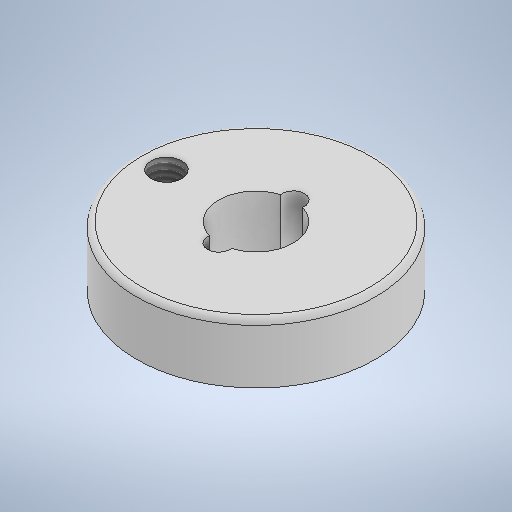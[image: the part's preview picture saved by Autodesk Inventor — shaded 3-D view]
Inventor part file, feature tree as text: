
AUTODESK INVENTOR PART (.ipt)
format: ipt  version: 2025.1 (Build 291241000, 241)  size: 259,072 bytes
history: native  units: mm
features: sketch x3, extrude x2, hole x1, fillet x1
ambient origin geometry x8: Origin, YZ Plane, XZ Plane, XY Plane, X Axis, Y Axis, Z Axis, Center Point
bodies: Solid1 (feature_tree)
feature tree (7):
  extrude  "Extrusion1"  Depth=10.0mm
  extrude  "Extrusion2"  Depth=8.0mm
  hole  "Hole1"  [1 undecoded]
  fillet  "Fillet1"  Radius=12.0mm
  sketch  "Sketch1"  dims[d0=32.0mm d1=10.0mm]
  sketch  "Sketch2"  dims[d2=8.0mm d3=0.0mm d4=3.0mm]
  sketch  "Sketch3"  dims[d5=3.0mm d6=8.0mm d7=0.0mm d8=12.0mm d9=4.134mm d10=10.0mm d11=4.0mm d12=2.0mm d13=90.0deg d14=14.2mm d15=0.0mm d16=0.75mm]
note: 1 required parameter value undecoded (feature->parameter linkage not recoverable at this tier; creation-order binding heuristic only, values carry confidence <= 0.55)
